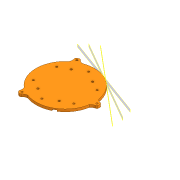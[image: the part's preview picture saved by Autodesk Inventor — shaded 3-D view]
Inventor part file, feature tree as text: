
AUTODESK INVENTOR PART (.ipt)
format: ipt  version: 2020.3 (Build 243373000, 373)  size: 325,120 bytes
history: native  units: mm
features: extrude x8, sketch x4, plane x3, fillet x2, pattern_circular x1
ambient origin geometry x8: Origin, YZ Plane, XZ Plane, XY Plane, X Axis, Y Axis, Z Axis, Center Point
bodies: Solid1 (feature_tree)
feature tree (18):
  sketch  "Sketch1"  dims[d0=95.0mm d1=120.0deg]
  extrude  "Extrusion1"  TaperAngle=120.0deg  [1 undecoded]
  plane  "Work Plane1"
  plane  "Work Plane2"
  plane  "Work Plane3"
  extrude  "Extrusion2"  Depth=16.0mm
  extrude  "Extrusion3"  Depth=6.0mm
  sketch  "Sketch2"  dims[d2=120.0deg d3=16.0mm]
  sketch  "Sketch3"  dims[d4=3.0mm d5=6.0mm]
  extrude  "Extrusion4"  Depth=10.0mm
  extrude  "Extrusion5"  Depth=10.0mm
  extrude  "Extrusion6"  Depth=10.0mm
  fillet  "Fillet1"  Radius=1.2mm
  fillet  "Fillet2"  Radius=4.0mm
  extrude  "Extrusion7"  Depth=10.0mm TaperAngle=360.0deg
  pattern_circular  "Circular Pattern1"  [2 undecoded]
  extrude  "Extrusion8"  Depth=10.0mm
  sketch  "Sketch4"  dims[d6=1.0mm d7=10.0mm d8=3.6mm d9=2.4mm d10=1.2mm d11=4.0mm d12=0.0mm d13=30.0mm d15=360.0deg d17=9.6mm d18=12.0mm d19=2.0mm d20=6.0mm d21=2.0mm d23=60.0deg d24=6.1mm d25=8.0mm d26=6.1mm d27=60.0deg d28=1.745329mm d29=1.745329mm d39=90.0deg d40=90.0deg d41=90.0deg d42=5.0mm d43=0.0mm d44=2.0mm d45=0.0mm d46=5.5mm d47=5.5mm d48=5.5mm d49=24.0mm d50=0.0mm d51=24.0mm d52=0.0mm d53=24.0mm d54=0.0mm d55=6.0mm d56=40.0mm d57=60.0mm d58=3.2mm d59=1.3mm d60=1.0mm d61=1.0mm d62=1.3mm d63=6.0mm d64=3.0mm d65=8.0mm d66=6.0mm d67=10.0mm d68=0.0mm d69=60.0mm d70=360.0deg d72=10.0mm d73=0.0mm d74=0.5mm d75=0.872665mm d76=0.5mm d77=0.872665mm]
note: 3 required parameter values undecoded (feature->parameter linkage not recoverable at this tier; creation-order binding heuristic only, values carry confidence <= 0.55)
